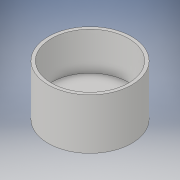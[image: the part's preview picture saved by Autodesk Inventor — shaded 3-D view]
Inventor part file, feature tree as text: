
AUTODESK INVENTOR PART (.ipt)
format: ipt  version: 2019.1 (Build 231200000, 200)  size: 254,976 bytes
history: native  units: in
note: dims shown in document units (in); Inventor stores cm internally (conversion verified against a paired STEP export)
features: extrude x3, sketch x3
ambient origin geometry x8: Origin, YZ Plane, XZ Plane, XY Plane, X Axis, Y Axis, Z Axis, Center Point
bodies: Solid1 (feature_tree)
feature tree (6):
  extrude  "Extrusion1"  Depth=0.25in
  extrude  "Extrusion2"  Depth=1.525in
  extrude  "Extrusion3"  Depth=0.75in
  sketch  "Sketch1"  dims[d0=1.65in d1=0.25in]
  sketch  "Sketch2"  dims[d2=0.0in d3=1.525in]
  sketch  "Sketch3"  dims[d4=1.65in d5=0.75in d6=0.0in d7=0.125in d8=0.0in]
